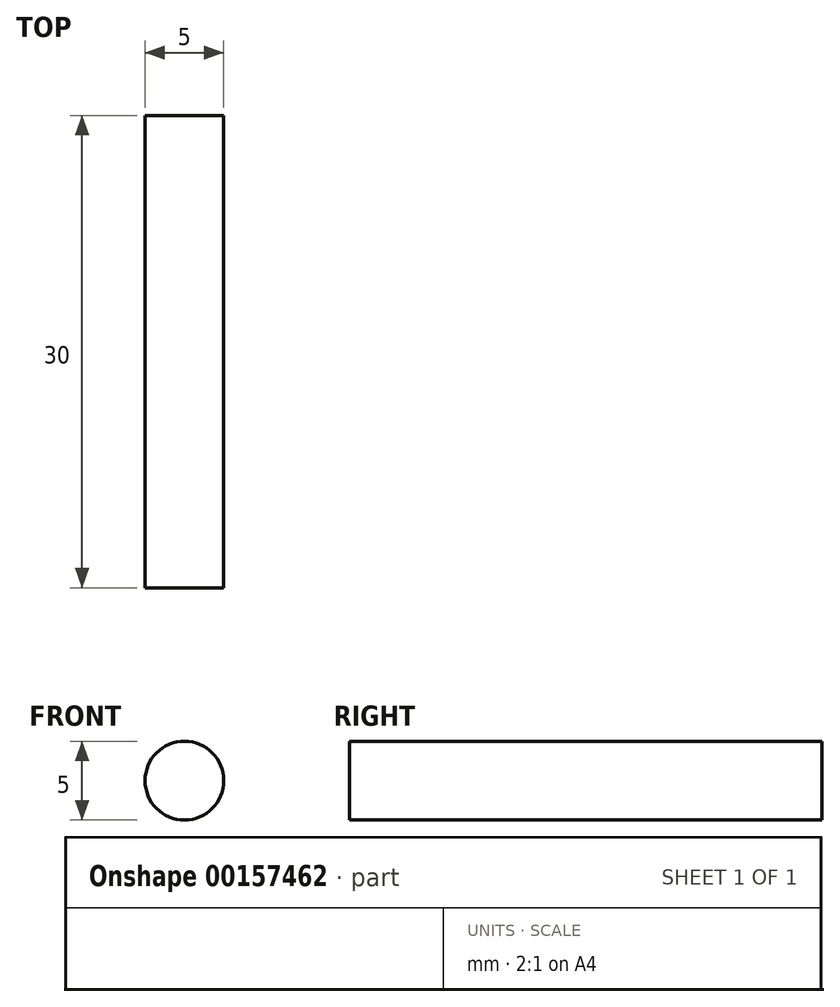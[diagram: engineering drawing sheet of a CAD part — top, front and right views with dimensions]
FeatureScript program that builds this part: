
annotation { "Feature Type Name" : "Feature", "Feature Type Description" : "" }
export const myFeature = defineFeature(function(context is Context, id is Id, definition is map)
    precondition{}
    {
        {
            var Q0;
            Q0=qCreatedBy(makeId("Front.planeOp"),FACE);
            var sketch = newSketch(context, id + "F0", { "sketchPlane" : qUnion([Q0])});
            skCircle(sketch, "E0", {"center": v(0, 0) * mm, "radius": 2.5 * mm});
            skSolve(sketch);
        }
        {
            var Q0;
            Q0=makeQuery(id+"F0.imprint","IMPRINT",FACE,{"disambiguationData":[TD([[makeQuery(id+"F0.imprint","IMPRINT",EDGE,{"derivedFrom":sQuery(id+"F0.wireOp",EDGE,"E0")}),1.0]])]});
            extrude(context, id + "F1", {"entities" : qUnion([Q0]), "depth" : 30 * mm});
        }
    });
